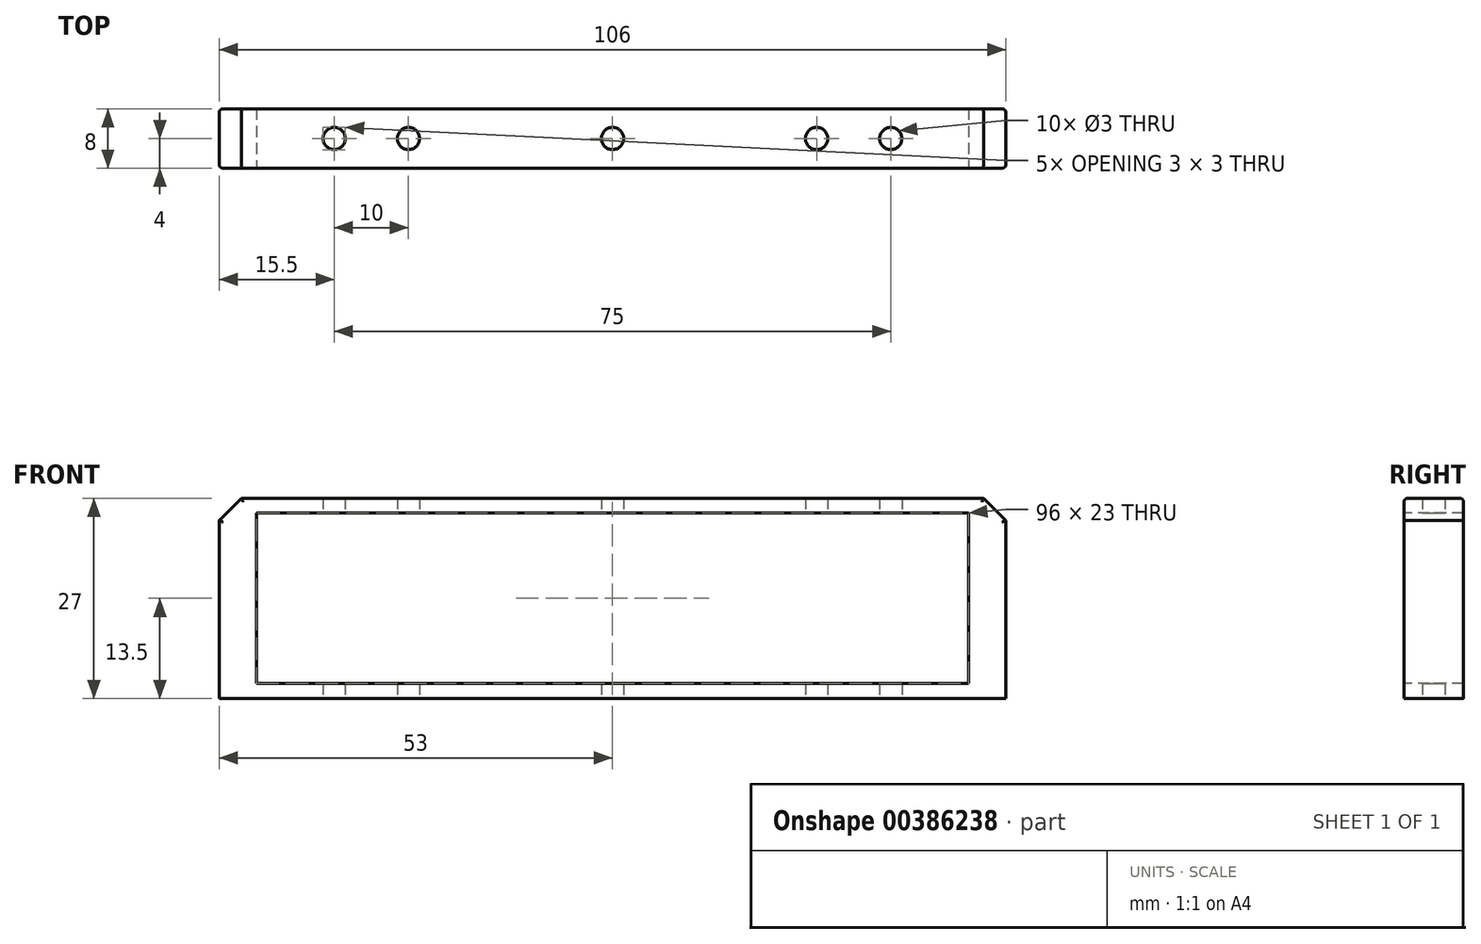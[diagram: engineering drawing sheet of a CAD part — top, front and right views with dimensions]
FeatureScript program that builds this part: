
annotation { "Feature Type Name" : "Feature", "Feature Type Description" : "" }
export const myFeature = defineFeature(function(context is Context, id is Id, definition is map)
    precondition{}
    {
        {
            assignVariable(context, id + "F0", {"name" : "height", "anyValue" : 27});
        }
        {
            var Q0;
            Q0=qCreatedBy(makeId("Top.planeOp"),FACE);
            var sketch = newSketch(context, id + "F1", { "sketchPlane" : qUnion([Q0])});
            skCircle(sketch, "E0", {"center": v(0, 0) * mm, "radius": 1.5 * mm});
            skCircle(sketch, "E1", {"center": v(37.5, 0) * mm, "radius": 1.5 * mm});
            skCircle(sketch, "E2", {"center": v(-37.5, 0) * mm, "radius": 1.5 * mm});
            skCircle(sketch, "E3", {"center": v(-27.5, 0) * mm, "radius": 1.5 * mm});
            skCircle(sketch, "E4", {"center": v(27.5, 0) * mm, "radius": 1.5 * mm});
            skLineSegment(sketch, "E5.bottom", {"start": v(-53, 4) * mm, "end": v(53, 4) * mm});
            skLineSegment(sketch, "E5.top", {"start": v(-53, -4) * mm, "end": v(53, -4) * mm});
            skLineSegment(sketch, "E5.left", {"start": v(-53, 4) * mm, "end": v(-53, -4) * mm});
            skLineSegment(sketch, "E5.right", {"start": v(53, 4) * mm, "end": v(53, -4) * mm});
            skSolve(sketch);
        }
        {
            var Q0;
            Q0=makeQuery(id+"F1.imprint","IMPRINT",FACE,{"disambiguationData":[TD([[makeQuery(id+"F1.imprint","IMPRINT",EDGE,{"derivedFrom":sQuery(id+"F1.wireOp",EDGE,"E0")}),-1.0]])]});
            var Q1;
            {var subQ0=sQuery(id+"F1.wireOp",EDGE,"E5.left");Q1=makeQuery(id+"F1.imprint","IMPRINT",FACE,{"disambiguationData":[TD([[makeQuery(id+"F1.imprint","IMPRINT",EDGE,{"derivedFrom":subQ0}),1.0]])]});}
            var Q2;
            {var subQ0=sQuery(id+"F1.wireOp",EDGE,"E5.right");Q2=makeQuery(id+"F1.imprint","IMPRINT",FACE,{"disambiguationData":[TD([[makeQuery(id+"F1.imprint","IMPRINT",EDGE,{"derivedFrom":subQ0}),-1.0]])]});}
            extrude(context, id + "F2", {"entities" : qUnion([Q0, Q1, Q2]), "depth" : (getVariable(context, 'height')) * mm});
        }
        {
            var Q0;
            Q0=makeQuery(id+"F2.opExtrude","SWEPT_FACE",FACE,{"disambiguationData":[OSD([sQuery(id+"F1.wireOp",EDGE,"E5.top")])]});
            var sketch = newSketch(context, id + "F3", { "sketchPlane" : qUnion([Q0])});
            skLineSegment(sketch, "E6.bottom", {"start": v(-48, 2) * mm, "end": v(48, 2) * mm});
            skLineSegment(sketch, "E6.top", {"start": v(-48, 25) * mm, "end": v(48, 25) * mm});
            skLineSegment(sketch, "E6.left", {"start": v(-48, 2) * mm, "end": v(-48, 25) * mm});
            skLineSegment(sketch, "E6.right", {"start": v(48, 2) * mm, "end": v(48, 25) * mm});
            skSolve(sketch);
        }
        {
            var Q0;
            Q0=makeQuery(id+"F3.imprint","IMPRINT",FACE,{"disambiguationData":[TD([[makeQuery(id+"F3.imprint","IMPRINT",EDGE,{"derivedFrom":sQuery(id+"F3.wireOp",EDGE,"E6.bottom")}),1.0]])]});
            extrude(context, id + "F4", {"entities" : qUnion([Q0]), "operationType" : NewBodyOperationType.REMOVE, "oppositeDirection" : true, "depth" : 25 * mm});
        }
        {
            var Q0;
            Q0=makeQuery(id+"F2.opExtrude","CAP_EDGE",EDGE,{"disambiguationData":[OSD([sQuery(id+"F1.wireOp",EDGE,"E5.left")])],"isStart":false});
            var Q1;
            Q1=makeQuery(id+"F2.opExtrude","CAP_EDGE",EDGE,{"disambiguationData":[OSD([sQuery(id+"F1.wireOp",EDGE,"E5.right")])],"isStart":false});
            chamfer(context, id + "F5", {"entities" : qUnion([Q0, Q1]), "width" : 3 * mm, "tangentPropagation" : true});
        }
        {
            var Q0;
            Q0=makeQuery(id+"F2.opExtrude","CAP_EDGE",EDGE,{"disambiguationData":[OSD([sQuery(id+"F1.wireOp",EDGE,"E5.top")])],"isStart":false});
            var Q1;
            Q1=makeQuery(id+"F2.opExtrude","CAP_EDGE",EDGE,{"disambiguationData":[OSD([sQuery(id+"F1.wireOp",EDGE,"E5.bottom")])],"isStart":false});
            var Q2;
            Q2=makeQuery(id+"F5.opChamfer","BLEND_EDGE",EDGE,{"blendedFrom":[makeQuery(id+"F2.opExtrude","CAP_EDGE",EDGE,{"disambiguationData":[OSD([sQuery(id+"F1.wireOp",EDGE,"E5.right")])],"isStart":false}),makeQuery(id+"F2.opExtrude","SWEPT_FACE",FACE,{"disambiguationData":[OSD([sQuery(id+"F1.wireOp",EDGE,"E5.top")])]})],"blendedInto":[makeQuery(id+"F2.opExtrude","SWEPT_FACE",FACE,{"disambiguationData":[OSD([sQuery(id+"F1.wireOp",EDGE,"E5.top")])]})]});
            var Q3;
            Q3=makeQuery(id+"F2.opExtrude","SWEPT_EDGE",EDGE,{"disambiguationData":[OSD([sQuery(id+"F1.wireOp",EDGE,"E5.top"),sQuery(id+"F1.wireOp",EDGE,"E5.right")])]});
            var Q4;
            Q4=makeQuery(id+"F5.opChamfer","BLEND_EDGE",EDGE,{"blendedFrom":[makeQuery(id+"F2.opExtrude","CAP_EDGE",EDGE,{"disambiguationData":[OSD([sQuery(id+"F1.wireOp",EDGE,"E5.right")])],"isStart":false}),makeQuery(id+"F2.opExtrude","SWEPT_FACE",FACE,{"disambiguationData":[OSD([sQuery(id+"F1.wireOp",EDGE,"E5.bottom")])]})],"blendedInto":[makeQuery(id+"F2.opExtrude","SWEPT_FACE",FACE,{"disambiguationData":[OSD([sQuery(id+"F1.wireOp",EDGE,"E5.bottom")])]})]});
            var Q5;
            Q5=makeQuery(id+"F2.opExtrude","SWEPT_EDGE",EDGE,{"disambiguationData":[OSD([sQuery(id+"F1.wireOp",EDGE,"E5.bottom"),sQuery(id+"F1.wireOp",EDGE,"E5.right")])]});
            var Q6;
            Q6=makeQuery(id+"F5.opChamfer","BLEND_EDGE",EDGE,{"blendedFrom":[makeQuery(id+"F2.opExtrude","CAP_EDGE",EDGE,{"disambiguationData":[OSD([sQuery(id+"F1.wireOp",EDGE,"E5.left")])],"isStart":false}),makeQuery(id+"F2.opExtrude","SWEPT_FACE",FACE,{"disambiguationData":[OSD([sQuery(id+"F1.wireOp",EDGE,"E5.top")])]})],"blendedInto":[makeQuery(id+"F2.opExtrude","SWEPT_FACE",FACE,{"disambiguationData":[OSD([sQuery(id+"F1.wireOp",EDGE,"E5.top")])]})]});
            var Q7;
            Q7=makeQuery(id+"F5.opChamfer","BLEND_EDGE",EDGE,{"blendedFrom":[makeQuery(id+"F2.opExtrude","CAP_EDGE",EDGE,{"disambiguationData":[OSD([sQuery(id+"F1.wireOp",EDGE,"E5.left")])],"isStart":false}),makeQuery(id+"F2.opExtrude","SWEPT_FACE",FACE,{"disambiguationData":[OSD([sQuery(id+"F1.wireOp",EDGE,"E5.bottom")])]})],"blendedInto":[makeQuery(id+"F2.opExtrude","SWEPT_FACE",FACE,{"disambiguationData":[OSD([sQuery(id+"F1.wireOp",EDGE,"E5.bottom")])]})]});
            var Q8;
            Q8=makeQuery(id+"F2.opExtrude","SWEPT_EDGE",EDGE,{"disambiguationData":[OSD([sQuery(id+"F1.wireOp",EDGE,"E5.top"),sQuery(id+"F1.wireOp",EDGE,"E5.left")])]});
            var Q9;
            Q9=makeQuery(id+"F2.opExtrude","SWEPT_EDGE",EDGE,{"disambiguationData":[OSD([sQuery(id+"F1.wireOp",EDGE,"E5.bottom"),sQuery(id+"F1.wireOp",EDGE,"E5.left")])]});
            fillet(context, id + "F6", {"entities" : qUnion([Q0, Q1, Q2, Q3, Q4, Q5, Q6, Q7, Q8, Q9]), "radius" : 0.5 * mm, "tangentPropagation" : true, "allowEdgeOverflow" : false});
        }
    });
